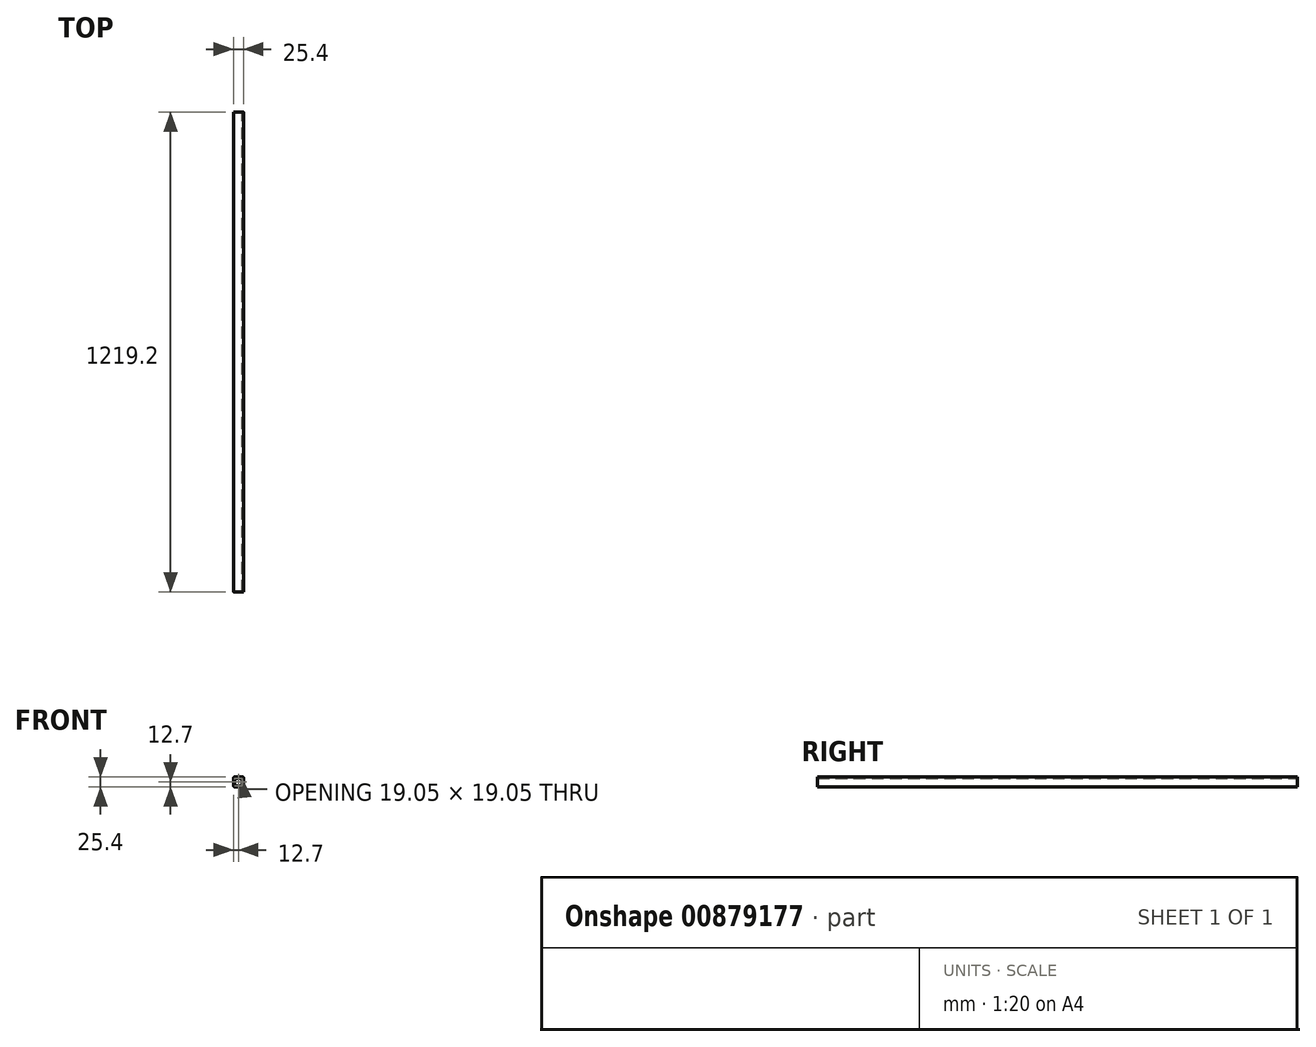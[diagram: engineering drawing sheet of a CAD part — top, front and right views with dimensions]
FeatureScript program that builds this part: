
annotation { "Feature Type Name" : "Feature", "Feature Type Description" : "" }
export const myFeature = defineFeature(function(context is Context, id is Id, definition is map)
    precondition{}
    {
        {
            var Q0;
            Q0=qCreatedBy(makeId("Front.planeOp"),FACE);
            var sketch = newSketch(context, id + "F0", { "sketchPlane" : qUnion([Q0])});
            skLineSegment(sketch, "E0.bottom", {"start": v(-3.18, 0) * mm, "end": v(-22.22, 0) * mm});
            skLineSegment(sketch, "E0.top", {"start": v(-3.18, 25.4) * mm, "end": v(-22.23, 25.4) * mm});
            skLineSegment(sketch, "E0.left", {"start": v(0, 3.18) * mm, "end": v(0, 22.23) * mm});
            skLineSegment(sketch, "E0.right", {"start": v(-25.4, 3.17) * mm, "end": v(-25.4, 22.22) * mm});
            skLineSegment(sketch, "E1.bottom", {"start": v(-6.35, 3.18) * mm, "end": v(-19.05, 3.18) * mm});
            skLineSegment(sketch, "E1.top", {"start": v(-6.35, 22.23) * mm, "end": v(-19.05, 22.23) * mm});
            skLineSegment(sketch, "E1.left", {"start": v(-3.18, 6.35) * mm, "end": v(-3.18, 19.05) * mm});
            skLineSegment(sketch, "E1.right", {"start": v(-22.23, 6.35) * mm, "end": v(-22.23, 19.05) * mm});
            skPoint(sketch, "E2.visualSharp", {"position": v(-3.18, 22.23) * mm});
            skArc(sketch, "E2.filletArc", {"start": v(-3.18, 19.05) * mm, "mid": v(-4.1, 21.3) * mm, "end": v(-6.35, 22.23) * mm});
            skPoint(sketch, "E3.visualSharp", {"position": v(-22.23, 22.23) * mm});
            skArc(sketch, "E3.filletArc", {"start": v(-19.05, 22.23) * mm, "mid": v(-21.3, 21.3) * mm, "end": v(-22.23, 19.05) * mm});
            skPoint(sketch, "E4.visualSharp", {"position": v(-22.23, 3.17) * mm});
            skArc(sketch, "E4.filletArc", {"start": v(-22.23, 6.35) * mm, "mid": v(-21.3, 4.1) * mm, "end": v(-19.05, 3.17) * mm});
            skPoint(sketch, "E5.visualSharp", {"position": v(-3.18, 3.18) * mm});
            skArc(sketch, "E5.filletArc", {"start": v(-6.35, 3.18) * mm, "mid": v(-4.1, 4.1) * mm, "end": v(-3.18, 6.35) * mm});
            skPoint(sketch, "E6.visualSharp", {"position": v(0, 25.4) * mm});
            skArc(sketch, "E6.filletArc", {"start": v(0, 22.23) * mm, "mid": v(-0.93, 24.47) * mm, "end": v(-3.18, 25.4) * mm});
            skPoint(sketch, "E7.visualSharp", {"position": v(-25.4, 25.4) * mm});
            skArc(sketch, "E7.filletArc", {"start": v(-22.23, 25.4) * mm, "mid": v(-24.47, 24.47) * mm, "end": v(-25.4, 22.22) * mm});
            skPoint(sketch, "E8.visualSharp", {"position": v(-25.4, 0) * mm});
            skArc(sketch, "E8.filletArc", {"start": v(-25.4, 3.17) * mm, "mid": v(-24.47, 0.93) * mm, "end": v(-22.22, 0) * mm});
            skPoint(sketch, "E9.visualSharp", {"position": v(0, 0) * mm});
            skArc(sketch, "E9.filletArc", {"start": v(-3.18, 0) * mm, "mid": v(-0.93, 0.93) * mm, "end": v(0, 3.18) * mm});
            skSolve(sketch);
        }
        {
            var Q0;
            Q0=qSketchRegion(id+"F0",true);
            extrude(context, id + "F1", {"entities" : qUnion([Q0]), "depth" : 1219.2 * mm, "offsetDistance" : 25.4 * mm});
        }
    });
